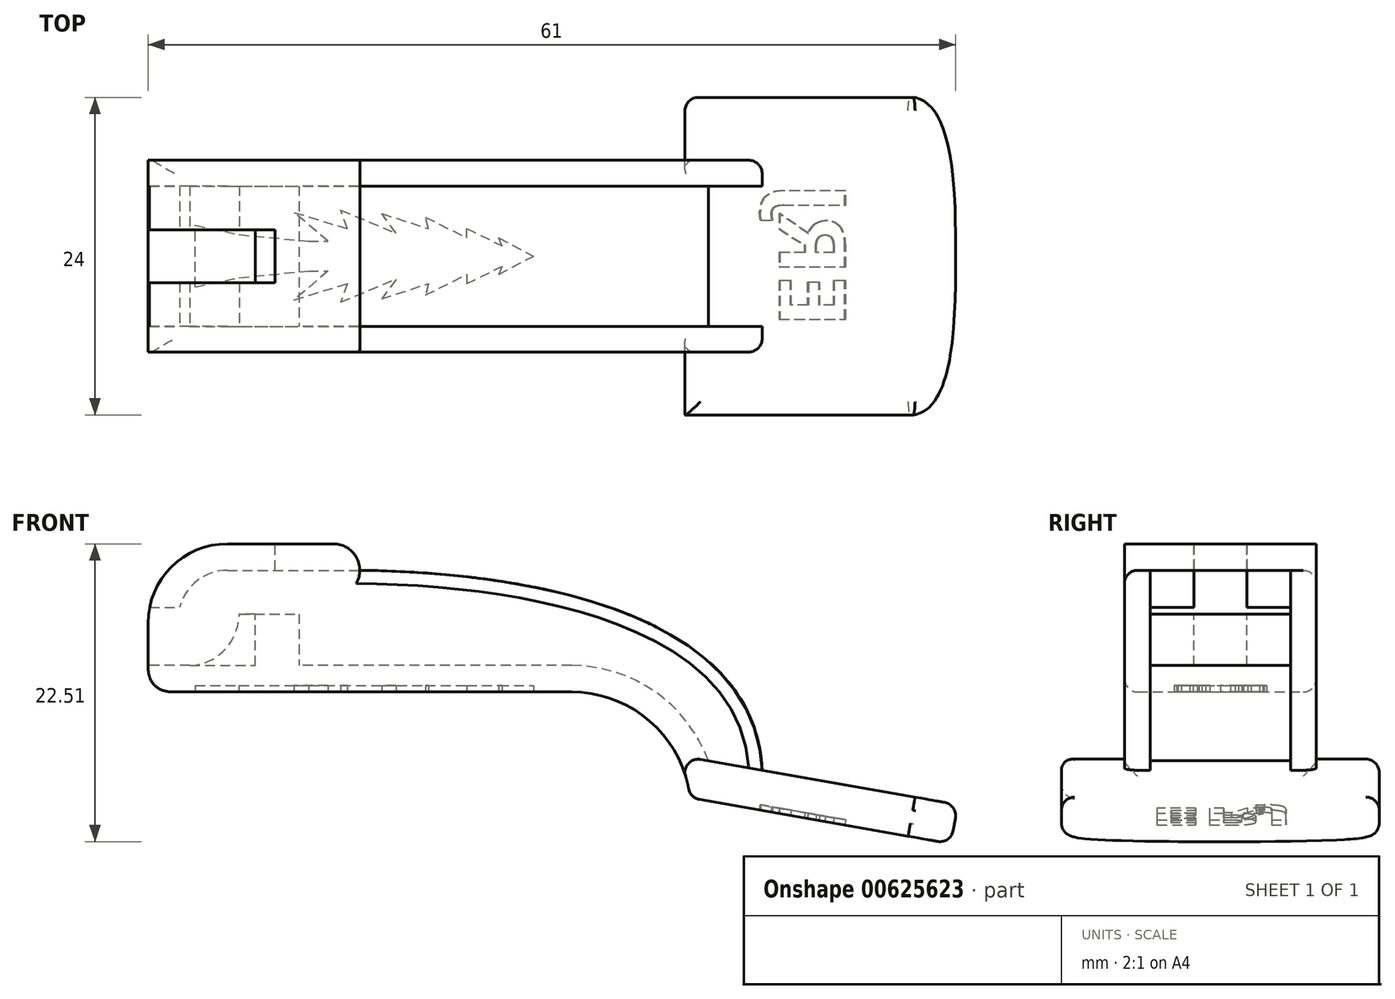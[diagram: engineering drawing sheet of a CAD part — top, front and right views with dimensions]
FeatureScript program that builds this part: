
annotation { "Feature Type Name" : "Feature", "Feature Type Description" : "" }
export const myFeature = defineFeature(function(context is Context, id is Id, definition is map)
    precondition{}
    {
        {
            var Q0;
            Q0=qCreatedBy(makeId("Front.planeOp"),FACE);
            var sketch = newSketch(context, id + "F0", { "sketchPlane" : qUnion([Q0])});
            skLineSegment(sketch, "E0", {"start": v(0, 0) * mm, "end": v(-32, 0) * mm});
            skArc(sketch, "E1", {"start": v(0, 0) * mm, "mid": v(6, -2.3) * mm, "end": v(8.94, -8) * mm});
            skLineSegment(sketch, "E2", {"start": v(8.94, -8) * mm, "end": v(28.64, -11.47) * mm});
            skLineSegment(sketch, "E3", {"start": v(8.94, -8) * mm, "end": v(8.94, -11.9) * mm, "construction": true});
            skLineSegment(sketch, "E4.0", {"start": v(14.39, -5.91) * mm, "end": v(29.16, -8.52) * mm});
            skLineSegment(sketch, "E5", {"start": v(28.64, -11.47) * mm, "end": v(29.16, -8.52) * mm});
            skLineSegment(sketch, "E6", {"start": v(-32, 0) * mm, "end": v(-32, 5.2) * mm});
            skLineSegment(sketch, "E7", {"start": v(-26, 11.2) * mm, "end": v(-18, 11.2) * mm});
            skArc(sketch, "E8", {"start": v(-18, 11.2) * mm, "mid": v(-16.59, 10.61) * mm, "end": v(-16, 9.2) * mm});
            skFitSpline(sketch, "E9", {"points": [v(-16, 9.2) * mm, v(14.39, -5.91) * mm], "startDerivative": vector(43.94, -0.56) * mm, "endDerivative": vector(1.38, -33.6) * mm});
            skLineSegment(sketch, "E10", {"start": v(14.39, -5.91) * mm, "end": v(7.95, -4.78) * mm});
            skPoint(sketch, "E11.visualSharp", {"position": v(-32, 11.2) * mm});
            skArc(sketch, "E11.filletArc", {"start": v(-26, 11.2) * mm, "mid": v(-30.24, 9.44) * mm, "end": v(-32, 5.2) * mm});
            skSolve(sketch);
        }
        {
            var Q0;
            Q0 = qSketchRegion(id + "F0", true);
            extrude(context, id + "F1", {"entities" : qUnion([Q0]), "endBound" : BoundingType.SYMMETRIC, "depth" : 14.5 * mm, "offsetDistance" : 25 * mm});
        }
        {
            var Q0;
            {var subQ0=sQuery(id+"F0.wireOp",EDGE,"E2");Q0=makeQuery(id+"F0.imprint","IMPRINT",FACE,{"disambiguationData":[TD([[makeQuery(id+"F0.imprint","IMPRINT",EDGE,{"derivedFrom":subQ0}),1.0]])]});}
            extrude(context, id + "F2", {"entities" : qUnion([Q0]), "operationType" : NewBodyOperationType.ADD, "endBound" : BoundingType.SYMMETRIC, "depth" : 24 * mm, "offsetDistance" : 25 * mm});
        }
        {
            var Q0;
            {var subQ0=sQuery(id+"F0.wireOp",EDGE,"E4.0");Q0=makeQuery(id+"F2.boolean.opBoolean","MERGE",FACE,{"derivedFrom":[makeQuery(id+"F1.opExtrude","SWEPT_FACE",FACE,{"disambiguationData":[OSD([subQ0])]}),makeQuery(id+"F2.opExtrude","SWEPT_FACE",FACE,{"disambiguationData":[OSD([subQ0,sQuery(id+"F0.wireOp",EDGE,"E10")])]})]});}
            var sketch = newSketch(context, id + "F3", { "sketchPlane" : qUnion([Q0])});
            skLineSegment(sketch, "E12", {"start": v(8.66, 7.25) * mm, "end": v(13.4, 12) * mm});
            skLineSegment(sketch, "E13.MirrorCS", {"start": v(8.66, -7.25) * mm, "end": v(13.4, -12) * mm});
            skFitSpline(sketch, "E14", {"points": [v(27.02, 12) * mm, v(30.2, 0) * mm], "startDerivative": vector(9.53, -1.6) * mm, "endDerivative": vector(0, -13.11) * mm});
            skFitSpline(sketch, "E15.MirrorCS", {"points": [v(27.02, -12) * mm, v(30.2, 0) * mm], "startDerivative": vector(9.53, 1.6) * mm, "endDerivative": vector(0, 13.11) * mm});
            skSolve(sketch);
        }
        {
            var Q0;
            Q0=qCreatedBy(makeId("Front.planeOp"),FACE);
            var sketch = newSketch(context, id + "F4", { "sketchPlane" : qUnion([Q0])});
            skLineSegment(sketch, "E16.0", {"start": v(0, 2) * mm, "end": v(-20.6, 2) * mm});
            skArc(sketch, "E16.1", {"start": v(0, 2) * mm, "mid": v(6.3, 0.02) * mm, "end": v(10.32, -5.2) * mm});
            skLineSegment(sketch, "E17.0", {"start": v(14.39, -5.91) * mm, "end": v(10.32, -5.2) * mm});
            skFitSpline(sketch, "E18.0", {"points": [v(-16, 9.2) * mm, v(-1.35, 9.01) * mm, v(13.93, 5.29) * mm, v(14.39, -5.91) * mm]});
            skPoint(sketch, "E19.orphan", {"position": v(7.95, -4.78) * mm});
            skLineSegment(sketch, "E20", {"start": v(-32, 6.4) * mm, "end": v(-32, 2) * mm});
            skPoint(sketch, "E21.orphan", {"position": v(-32, 0) * mm});
            skLineSegment(sketch, "E22", {"start": v(-32, 6.4) * mm, "end": v(-29.6, 6.4) * mm});
            skLineSegment(sketch, "E23", {"start": v(-26, 9.2) * mm, "end": v(-16, 9.2) * mm});
            skLineSegment(sketch, "E24.0", {"start": v(-32, 2) * mm, "end": v(-32, 6.4) * mm});
            skPoint(sketch, "E25.orphan", {"position": v(-32, 5.2) * mm});
            skPoint(sketch, "E26.endSnap0", {"position": v(-16, 2) * mm});
            skLineSegment(sketch, "E27", {"start": v(-25.1, 5.9) * mm, "end": v(-20.6, 5.9) * mm});
            skLineSegment(sketch, "E28", {"start": v(-20.6, 5.9) * mm, "end": v(-20.6, 2) * mm});
            skFitSpline(sketch, "E29", {"points": [v(-28.84, 2) * mm, v(-25.1, 5.9) * mm], "startDerivative": vector(7.1, 0.36) * mm, "endDerivative": vector(0.12, 5.55) * mm});
            skLineSegment(sketch, "E30", {"start": v(-28.84, 2) * mm, "end": v(-32, 2) * mm});
            skArc(sketch, "E31", {"start": v(-26, 9.2) * mm, "mid": v(-28.28, 8.42) * mm, "end": v(-29.6, 6.4) * mm});
            skSolve(sketch);
        }
        {
            var Q0;
            Q0=makeQuery(id+"F4.imprint","IMPRINT",FACE,{"disambiguationData":[TD([[makeQuery(id+"F4.imprint","IMPRINT",EDGE,{"derivedFrom":sQuery(id+"F4.wireOp",EDGE,"E16.0")}),-1.0]])]});
            extrude(context, id + "F5", {"entities" : qUnion([Q0]), "operationType" : NewBodyOperationType.REMOVE, "endBound" : BoundingType.SYMMETRIC, "oppositeDirection" : true, "depth" : 10.6 * mm, "offsetDistance" : 25 * mm});
        }
        {
            var Q0;
            Q0=qCreatedBy(makeId("Front.planeOp"),FACE);
            var sketch = newSketch(context, id + "F6", { "sketchPlane" : qUnion([Q0])});
            skLineSegment(sketch, "E32.2", {"start": v(-26, 9.2) * mm, "end": v(-22.4, 9.2) * mm});
            skLineSegment(sketch, "E32.3", {"start": v(-32, 6.4) * mm, "end": v(-29.6, 6.4) * mm});
            skLineSegment(sketch, "E32.4", {"start": v(-32, 5.2) * mm, "end": v(-32, 6.4) * mm});
            skArc(sketch, "E32.5", {"start": v(-26, 11.2) * mm, "mid": v(-30.24, 9.44) * mm, "end": v(-32, 5.2) * mm});
            skLineSegment(sketch, "E32.6", {"start": v(-26, 11.2) * mm, "end": v(-22.4, 11.2) * mm});
            skPoint(sketch, "E33.orphan", {"position": v(-32, 0) * mm});
            skLineSegment(sketch, "E34", {"start": v(-22.4, 9.2) * mm, "end": v(-22.4, 11.2) * mm});
            skLineSegment(sketch, "E35", {"start": v(-32, 5.2) * mm, "end": v(-32, 13.03) * mm, "construction": true});
            skPoint(sketch, "E32.7.end.orphan", {"position": v(-16, 9.2) * mm});
            skPoint(sketch, "E32.7.start.orphan", {"position": v(-18, 11.2) * mm});
            skArc(sketch, "E36.0", {"start": v(-26, 9.2) * mm, "mid": v(-28.28, 8.42) * mm, "end": v(-29.6, 6.4) * mm});
            skSolve(sketch);
        }
        {
            var Q0;
            Q0=makeQuery(id+"F6.imprint","IMPRINT",FACE,{"disambiguationData":[TD([[makeQuery(id+"F6.imprint","IMPRINT",EDGE,{"derivedFrom":sQuery(id+"F6.wireOp",EDGE,"E32.0")}),1.0]])]});
            var Q1;
            Q1=makeQuery(id+"F6.imprint","IMPRINT",FACE,{"disambiguationData":[TD([[makeQuery(id+"F6.imprint","IMPRINT",EDGE,{"derivedFrom":sQuery(id+"F6.wireOp",EDGE,"E32.2")}),1.0]])]});
            extrude(context, id + "F7", {"entities" : qUnion([Q0, Q1]), "operationType" : NewBodyOperationType.REMOVE, "endBound" : BoundingType.SYMMETRIC, "oppositeDirection" : true, "depth" : 4 * mm, "offsetDistance" : 25 * mm});
        }
        {
            var Q0;
            Q0=qCreatedBy(makeId("Front.planeOp"),FACE);
            var sketch = newSketch(context, id + "F8", { "sketchPlane" : qUnion([Q0])});
            skLineSegment(sketch, "E37.0", {"start": v(-28.84, 6.4) * mm, "end": v(-25.1, 6.4) * mm});
            skLineSegment(sketch, "E38", {"start": v(-28.84, 2) * mm, "end": v(-28.84, 6.4) * mm});
            skLineSegment(sketch, "E39", {"start": v(-25.1, 6.4) * mm, "end": v(-23.9, 6.4) * mm});
            skLineSegment(sketch, "E40", {"start": v(-28.84, 2) * mm, "end": v(-23.9, 2) * mm});
            skLineSegment(sketch, "E41", {"start": v(-23.9, 2) * mm, "end": v(-23.9, 6.4) * mm});
            skSolve(sketch);
        }
        {
            var Q0;
            Q0=makeQuery(id+"F8.imprint","IMPRINT",FACE,{"disambiguationData":[TD([[makeQuery(id+"F8.imprint","IMPRINT",EDGE,{"derivedFrom":sQuery(id+"F8.wireOp",EDGE,"E37.0")}),-1.0]])]});
            extrude(context, id + "F9", {"entities" : qUnion([Q0]), "operationType" : NewBodyOperationType.REMOVE, "endBound" : BoundingType.SYMMETRIC, "oppositeDirection" : true, "depth" : 4 * mm, "offsetDistance" : 25 * mm});
        }
        {
            var Q0;
            Q0=makeQuery(id+"F1.opExtrude","CAP_EDGE",EDGE,{"disambiguationData":[OSD([sQuery(id+"F0.wireOp",EDGE,"E0")])],"isStart":false});
            var Q1;
            Q1=makeQuery(id+"F1.opExtrude","CAP_EDGE",EDGE,{"disambiguationData":[OSD([sQuery(id+"F0.wireOp",EDGE,"E0")])],"isStart":true});
            var Q2;
            Q2=makeQuery(id+"F2.opExtrude","CAP_EDGE",EDGE,{"disambiguationData":[OSD([sQuery(id+"F0.wireOp",EDGE,"E1")])],"isStart":true});
            var Q3;
            Q3=makeQuery(id+"F2.opExtrude","CAP_EDGE",EDGE,{"disambiguationData":[OSD([sQuery(id+"F0.wireOp",EDGE,"E5")])],"isStart":true});
            var Q4;
            Q4=makeQuery(id+"F2.opExtrude","CAP_EDGE",EDGE,{"disambiguationData":[OSD([sQuery(id+"F0.wireOp",EDGE,"E2")])],"isStart":true});
            var Q5;
            Q5=makeQuery(id+"F2.opExtrude","CAP_EDGE",EDGE,{"disambiguationData":[OSD([sQuery(id+"F0.wireOp",EDGE,"E4.0"),sQuery(id+"F0.wireOp",EDGE,"E10")])],"isStart":true});
            var Q6;
            {var subQ0=sQuery(id+"F0.wireOp",EDGE,"E2");var subQ1=sQuery(id+"F0.wireOp",EDGE,"E1");Q6=makeQuery(id+"F2.boolean.opBoolean","MERGE",EDGE,{"derivedFrom":[makeQuery(id+"F1.opExtrude","SWEPT_EDGE",EDGE,{"disambiguationData":[OSD([subQ1,subQ0])]}),makeQuery(id+"F2.opExtrude","SWEPT_EDGE",EDGE,{"disambiguationData":[OSD([subQ1,subQ0])]})]});}
            var Q7;
            Q7=makeQuery(id+"F2.opExtrude","CAP_EDGE",EDGE,{"disambiguationData":[OSD([sQuery(id+"F0.wireOp",EDGE,"E2")])],"isStart":false});
            var Q8;
            Q8=makeQuery(id+"F2.opExtrude","CAP_EDGE",EDGE,{"disambiguationData":[OSD([sQuery(id+"F0.wireOp",EDGE,"E4.0"),sQuery(id+"F0.wireOp",EDGE,"E10")])],"isStart":false});
            var Q9;
            {var subQ0=sQuery(id+"F0.wireOp",EDGE,"E1");var subQ1=sQuery(id+"F0.wireOp",EDGE,"E4.0");var subQ2=sQuery(id+"F0.wireOp",EDGE,"E5");var subQ3=sQuery(id+"F0.wireOp",EDGE,"E2");var subQ4=sQuery(id+"F0.wireOp",EDGE,"E10");Q9=makeQuery(id+"F2.boolean.opBoolean","SPLIT",EDGE,{"disambiguationData":[TD([makeQuery(id+"F2.opExtrude","CAP_FACE",FACE,{"disambiguationData":[OSD([subQ0,subQ3,subQ1,subQ2,subQ4])],"isStart":false})])],"derivedFrom":makeQuery(id+"F2.opExtrude","SWEPT_EDGE",EDGE,{"disambiguationData":[OSD([subQ0,subQ4])]})});}
            var Q10;
            {var subQ0=sQuery(id+"F0.wireOp",EDGE,"E4.0");var subQ1=sQuery(id+"F0.wireOp",EDGE,"E10");var subQ2=sQuery(id+"F0.wireOp",EDGE,"E5");var subQ3=sQuery(id+"F0.wireOp",EDGE,"E2");var subQ4=sQuery(id+"F0.wireOp",EDGE,"E1");Q10=makeQuery(id+"F2.boolean.opBoolean","SPLIT",EDGE,{"disambiguationData":[TD([makeQuery(id+"F2.opExtrude","CAP_FACE",FACE,{"disambiguationData":[OSD([subQ4,subQ3,subQ0,subQ2,subQ1])],"isStart":true})])],"derivedFrom":makeQuery(id+"F2.opExtrude","SWEPT_EDGE",EDGE,{"disambiguationData":[OSD([subQ4,subQ1])]})});}
            var Q11;
            Q11=makeQuery(id+"F1.opExtrude","CAP_EDGE",EDGE,{"disambiguationData":[OSD([sQuery(id+"F0.wireOp",EDGE,"E9")])],"isStart":false});
            var Q12;
            Q12=makeQuery(id+"F1.opExtrude","CAP_EDGE",EDGE,{"disambiguationData":[OSD([sQuery(id+"F0.wireOp",EDGE,"E9")])],"isStart":true});
            fillet(context, id + "F10", {"entities" : qUnion([Q0, Q1, Q2, Q3, Q4, Q5, Q6, Q7, Q8, Q9, Q10, Q11, Q12]), "radius" : 1 * mm, "tangentPropagation" : true, "allowEdgeOverflow" : false});
        }
        {
            var Q0;
            Q0=makeQuery(id+"F1.opExtrude","SWEPT_EDGE",EDGE,{"disambiguationData":[OSD([sQuery(id+"F0.wireOp",EDGE,"E0"),sQuery(id+"F0.wireOp",EDGE,"E6")])]});
            fillet(context, id + "F11", {"entities" : qUnion([Q0]), "radius" : 2 * mm, "rho" : 0.5, "crossSection" : FilletCrossSection.CONIC, "allowEdgeOverflow" : false});
        }
        {
            var Q0;
            {var subQ0=sQuery(id+"F3.wireOp",EDGE,"E14");Q0=makeQuery(id+"F3.imprint","IMPRINT",FACE,{"disambiguationData":[TD([[makeQuery(id+"F3.imprint","IMPRINT",EDGE,{"derivedFrom":subQ0}),1.0]])]});}
            var Q1;
            {var subQ0=sQuery(id+"F3.wireOp",EDGE,"E15.MirrorCS");Q1=makeQuery(id+"F3.imprint","IMPRINT",FACE,{"disambiguationData":[TD([[makeQuery(id+"F3.imprint","IMPRINT",EDGE,{"derivedFrom":subQ0}),-1.0]])]});}
            extrude(context, id + "F12", {"entities" : qUnion([Q0, Q1]), "operationType" : NewBodyOperationType.REMOVE, "endBound" : BoundingType.THROUGH_ALL, "oppositeDirection" : true, "depth" : 25 * mm, "offsetDistance" : 25 * mm});
        }
        {
            var Q0;
            {var subQ0=sQuery(id+"F0.wireOp",EDGE,"E2");Q0=makeQuery(id+"F12.boolean.opBoolean","INTERSECT",EDGE,{"derivedFrom":[makeQuery(id+"F2.boolean.opBoolean","MERGE",FACE,{"derivedFrom":[makeQuery(id+"F1.opExtrude","SWEPT_FACE",FACE,{"disambiguationData":[OSD([subQ0])]}),makeQuery(id+"F2.opExtrude","SWEPT_FACE",FACE,{"disambiguationData":[OSD([subQ0])]})]}),makeQuery(id+"F12.opExtrude","SWEPT_FACE",FACE,{"disambiguationData":[OSD([sQuery(id+"F3.wireOp",EDGE,"E14")])]})]});}
            var Q1;
            Q1=makeQuery(id+"F12.boolean.opBoolean","COPY",EDGE,{"derivedFrom":makeQuery(id+"F12.opExtrude","CAP_EDGE",EDGE,{"disambiguationData":[OSD([sQuery(id+"F3.wireOp",EDGE,"E15.MirrorCS")])],"isStart":true})});
            fillet(context, id + "F13", {"entities" : qUnion([Q0, Q1]), "radius" : 1 * mm, "tangentPropagation" : true, "allowEdgeOverflow" : false});
        }
        {
            var Q0;
            {var subQ0=sQuery(id+"F0.wireOp",EDGE,"E2");Q0=makeQuery(id+"F2.boolean.opBoolean","MERGE",FACE,{"derivedFrom":[makeQuery(id+"F1.opExtrude","SWEPT_FACE",FACE,{"disambiguationData":[OSD([subQ0])]}),makeQuery(id+"F2.opExtrude","SWEPT_FACE",FACE,{"disambiguationData":[OSD([subQ0])]})]});}
            var sketch = newSketch(context, id + "F14", { "sketchPlane" : qUnion([Q0])});
            skText(sketch, "E42", { "text": "ERJ", "fontName": "OpenSans-Bold.ttf"});
            skLineSegment(sketch, "E43", {"start": v(23.89, 0) * mm, "end": v(15.7, 0) * mm, "construction": true});
            const initialGuessF14  = {"E42": [0.01701, 0.00541, 0, -1, 0.0051]};
            skSetInitialGuess(sketch, initialGuessF14);
            skSolve(sketch);
        }
        {
            var Q0;
            Q0=makeQuery(id+"F14.imprint","IMPRINT",FACE,{"disambiguationData":[TD([[makeQuery(id+"F14.imprint","IMPRINT",EDGE,{"derivedFrom":sQuery(id+"F14.wireOp",EDGE,"E42.sketch_text.stroke-0")}),-1.0]])]});
            var Q1;
            Q1=makeQuery(id+"F14.imprint","IMPRINT",FACE,{"disambiguationData":[TD([[makeQuery(id+"F14.imprint","IMPRINT",EDGE,{"derivedFrom":sQuery(id+"F14.wireOp",EDGE,"E42.sketch_text.stroke-12")}),-1.0]])]});
            var Q2;
            Q2=makeQuery(id+"F14.imprint","IMPRINT",FACE,{"disambiguationData":[TD([[makeQuery(id+"F14.imprint","IMPRINT",EDGE,{"derivedFrom":sQuery(id+"F14.wireOp",EDGE,"E42.sketch_text.stroke-31")}),-1.0]])]});
            extrude(context, id + "F15", {"entities" : qUnion([Q0, Q1, Q2]), "operationType" : NewBodyOperationType.REMOVE, "oppositeDirection" : true, "depth" : .4 * mm, "offsetDistance" : 25 * mm});
        }
        {
            var Q0;
            Q0=makeQuery(id+"F1.opExtrude","SWEPT_FACE",FACE,{"disambiguationData":[OSD([sQuery(id+"F0.wireOp",EDGE,"E0")])]});
            var sketch = newSketch(context, id + "F16", { "sketchPlane" : qUnion([Q0])});
            skLineSegment(sketch, "E44", {"start": v(-28.43, 2.33) * mm, "end": v(-25.12, 1.63) * mm});
            skLineSegment(sketch, "E45", {"start": v(-25.12, 1.63) * mm, "end": v(-19.87, 1.12) * mm});
            skLineSegment(sketch, "E46", {"start": v(-19.87, 1.12) * mm, "end": v(-18.39, 1.12) * mm});
            skLineSegment(sketch, "E47", {"start": v(-18.39, 1.12) * mm, "end": v(-20.96, 3.3) * mm});
            skLineSegment(sketch, "E48", {"start": v(-20.96, 3.3) * mm, "end": v(-16.93, 2.07) * mm});
            skLineSegment(sketch, "E49", {"start": v(-16.93, 2.07) * mm, "end": v(-17.44, 3.49) * mm});
            skLineSegment(sketch, "E50", {"start": v(-17.44, 3.49) * mm, "end": v(-13.26, 1.74) * mm});
            skLineSegment(sketch, "E51", {"start": v(-13.26, 1.74) * mm, "end": v(-14.34, 3.22) * mm});
            skLineSegment(sketch, "E52", {"start": v(-14.34, 3.22) * mm, "end": v(-10.8, 2.07) * mm});
            skLineSegment(sketch, "E53", {"start": v(-10.8, 2.07) * mm, "end": v(-11.04, 2.95) * mm});
            skLineSegment(sketch, "E54", {"start": v(-11.04, 2.95) * mm, "end": v(-7.92, 1.38) * mm});
            skLineSegment(sketch, "E55", {"start": v(-7.92, 1.38) * mm, "end": v(-7.92, 2.07) * mm});
            skLineSegment(sketch, "E56", {"start": v(-7.92, 2.07) * mm, "end": v(-5.25, 0.78) * mm});
            skLineSegment(sketch, "E57", {"start": v(-5.25, 0.78) * mm, "end": v(-5.5, 1.38) * mm});
            skLineSegment(sketch, "E58", {"start": v(-5.5, 1.38) * mm, "end": v(-2.88, 0) * mm});
            skLineSegment(sketch, "E59", {"start": v(-28.43, 2.33) * mm, "end": v(-28.43, 0) * mm});
            skLineSegment(sketch, "E60.MirrorCS", {"start": v(-5.25, -0.78) * mm, "end": v(-5.5, -1.38) * mm});
            skLineSegment(sketch, "E61.MirrorCS", {"start": v(-10.8, -2.07) * mm, "end": v(-11.04, -2.95) * mm});
            skLineSegment(sketch, "E62.MirrorCS", {"start": v(-7.92, -1.38) * mm, "end": v(-7.92, -2.07) * mm});
            skLineSegment(sketch, "E63.MirrorCS", {"start": v(-7.92, -2.07) * mm, "end": v(-5.25, -0.78) * mm});
            skLineSegment(sketch, "E64.MirrorCS", {"start": v(-28.43, -2.33) * mm, "end": v(-25.12, -1.63) * mm});
            skLineSegment(sketch, "E65.MirrorCS", {"start": v(-25.12, -1.63) * mm, "end": v(-19.87, -1.12) * mm});
            skLineSegment(sketch, "E66.MirrorCS", {"start": v(-14.34, -3.22) * mm, "end": v(-10.8, -2.07) * mm});
            skLineSegment(sketch, "E67.MirrorCS", {"start": v(-13.26, -1.74) * mm, "end": v(-14.34, -3.22) * mm});
            skLineSegment(sketch, "E68.MirrorCS", {"start": v(-11.04, -2.95) * mm, "end": v(-7.92, -1.38) * mm});
            skLineSegment(sketch, "E69.MirrorCS", {"start": v(-19.87, -1.12) * mm, "end": v(-18.39, -1.12) * mm});
            skLineSegment(sketch, "E70.MirrorCS", {"start": v(-20.96, -3.3) * mm, "end": v(-16.93, -2.07) * mm});
            skLineSegment(sketch, "E71.MirrorCS", {"start": v(-18.39, -1.12) * mm, "end": v(-20.96, -3.3) * mm});
            skLineSegment(sketch, "E72.MirrorCS", {"start": v(-17.44, -3.49) * mm, "end": v(-13.26, -1.74) * mm});
            skLineSegment(sketch, "E73.MirrorCS", {"start": v(-16.93, -2.07) * mm, "end": v(-17.44, -3.49) * mm});
            skLineSegment(sketch, "E74.MirrorCS", {"start": v(-5.5, -1.38) * mm, "end": v(-2.88, 0) * mm});
            skLineSegment(sketch, "E75.MirrorCS", {"start": v(-28.43, -2.33) * mm, "end": v(-28.43, 0) * mm});
            skSolve(sketch);
        }
        {
            var Q0;
            Q0 = qSketchRegion(id + "F16", true);
            var Q1;
            Q1=makeQuery(id+"F16.imprint","IMPRINT",FACE,{"disambiguationData":[TD([[makeQuery(id+"F16.imprint","IMPRINT",EDGE,{"derivedFrom":sQuery(id+"F16.wireOp",EDGE,"E44")}),-1.0]])]});
            extrude(context, id + "F17", {"entities" : qUnion([Q0, Q1]), "operationType" : NewBodyOperationType.REMOVE, "oppositeDirection" : true, "depth" : .5 * mm, "offsetDistance" : 25 * mm});
        }
    });
